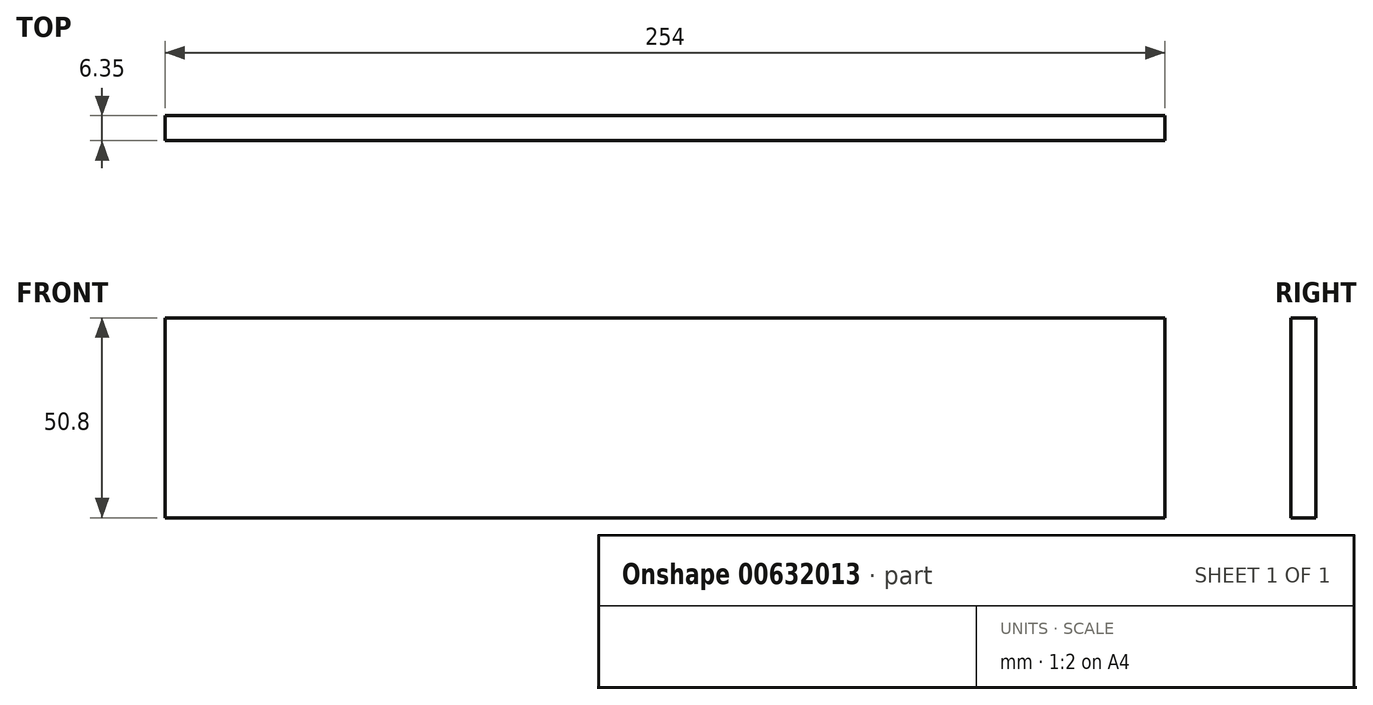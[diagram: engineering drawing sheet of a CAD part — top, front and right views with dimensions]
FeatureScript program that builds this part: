
annotation { "Feature Type Name" : "Feature", "Feature Type Description" : "" }
export const myFeature = defineFeature(function(context is Context, id is Id, definition is map)
    precondition{}
    {
        {
            var Q0;
            Q0=qCreatedBy(makeId("Front.planeOp"),FACE);
            var sketch = newSketch(context, id + "F0", { "sketchPlane" : qUnion([Q0])});
            skLineSegment(sketch, "E0.bottom", {"start": v(127, 25.4) * mm, "end": v(-127, 25.4) * mm});
            skLineSegment(sketch, "E0.top", {"start": v(127, -25.4) * mm, "end": v(-127, -25.4) * mm});
            skLineSegment(sketch, "E0.left", {"start": v(127, 25.4) * mm, "end": v(127, -25.4) * mm});
            skLineSegment(sketch, "E0.right", {"start": v(-127, 25.4) * mm, "end": v(-127, -25.4) * mm});
            skPoint(sketch, "E0.middle", {"position": v(0, 0) * mm});
            skSolve(sketch);
        }
        {
            var Q0;
            Q0=makeQuery(id+"F0.imprint","IMPRINT",FACE,{"disambiguationData":[TD([[makeQuery(id+"F0.imprint","IMPRINT",EDGE,{"derivedFrom":sQuery(id+"F0.wireOp",EDGE,"E0.bottom")}),1.0]])]});
            extrude(context, id + "F1", {"entities" : qUnion([Q0]), "depth" : 6.35 * mm, "offsetDistance" : 25.4 * mm});
        }
    });
